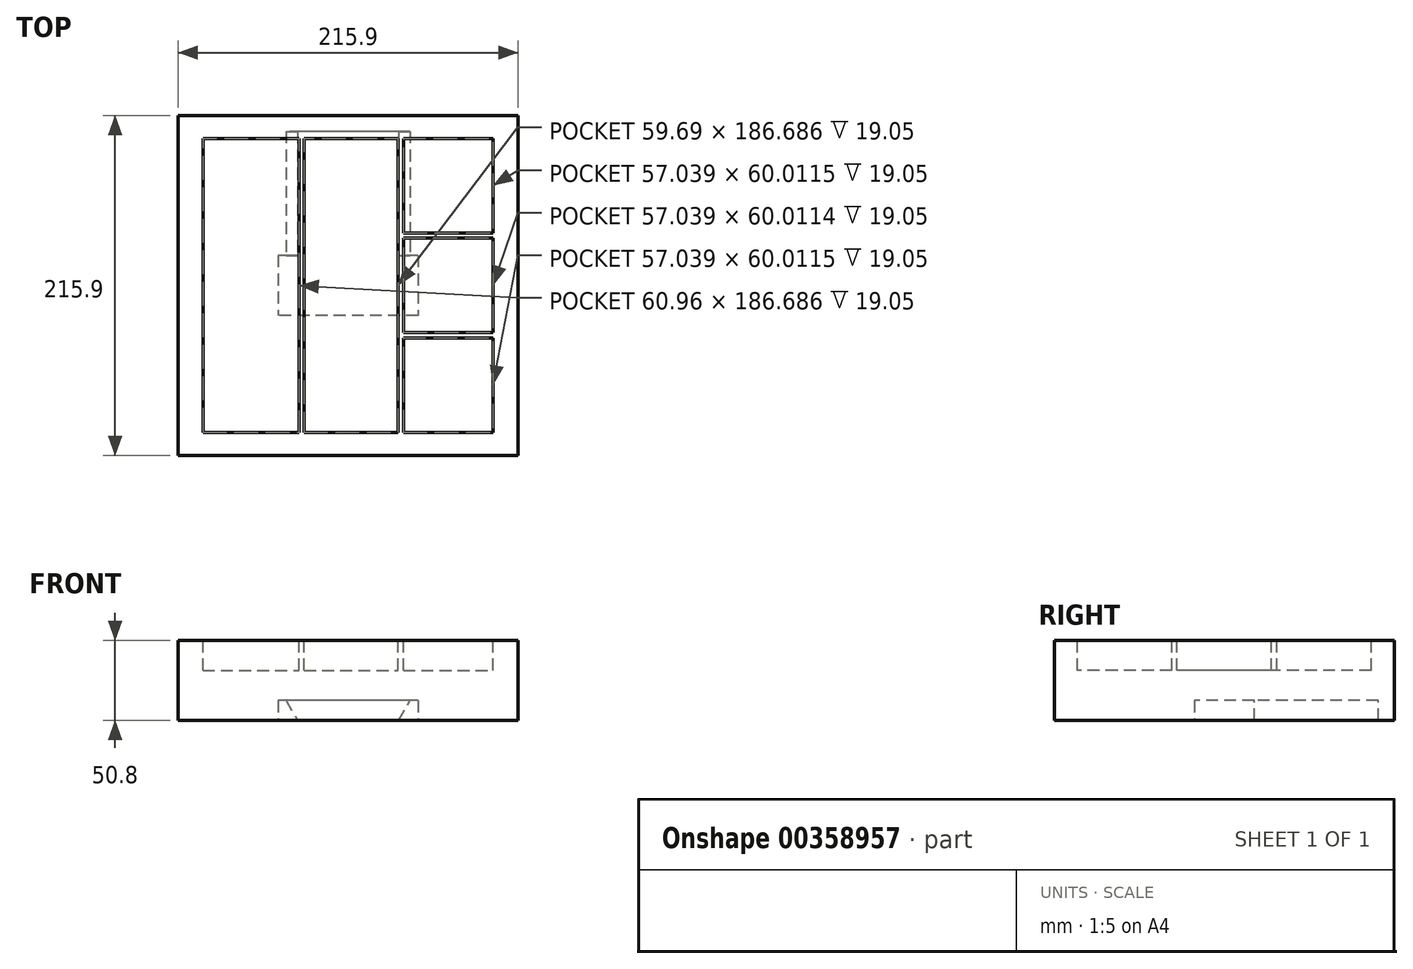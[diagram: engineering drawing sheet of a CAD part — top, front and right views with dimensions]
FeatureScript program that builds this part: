
annotation { "Feature Type Name" : "Feature", "Feature Type Description" : "" }
export const myFeature = defineFeature(function(context is Context, id is Id, definition is map)
    precondition{}
    {
        {
            var Q0;
            Q0=qCreatedBy(makeId("Top.planeOp"),FACE);
            var sketch = newSketch(context, id + "F0", { "sketchPlane" : qUnion([Q0])});
            skLineSegment(sketch, "E0.bottom", {"start": v(-107.95, 107.95) * mm, "end": v(107.95, 107.95) * mm});
            skLineSegment(sketch, "E0.top", {"start": v(-107.95, -107.95) * mm, "end": v(107.95, -107.95) * mm});
            skLineSegment(sketch, "E0.left", {"start": v(-107.95, 107.95) * mm, "end": v(-107.95, -107.95) * mm});
            skLineSegment(sketch, "E0.right", {"start": v(107.95, 107.95) * mm, "end": v(107.95, -107.95) * mm});
            skPoint(sketch, "E0.middle", {"position": v(0, 0) * mm});
            skSolve(sketch);
        }
        {
            var Q0;
            Q0 = qSketchRegion(id + "F0", true);
            extrude(context, id + "F1", {"entities" : qUnion([Q0]), "depth" : 50.8 * mm});
        }
        {
            var Q0;
            Q0=makeQuery(id+"F1.opExtrude","CAP_FACE",FACE,{"disambiguationData":[OSD([sQuery(id+"F0.wireOp",EDGE,"E0.bottom"),sQuery(id+"F0.wireOp",EDGE,"E0.top"),sQuery(id+"F0.wireOp",EDGE,"E0.left"),sQuery(id+"F0.wireOp",EDGE,"E0.right")])],"isStart":false});
            var sketch = newSketch(context, id + "F2", { "sketchPlane" : qUnion([Q0])});
            skLineSegment(sketch, "E1.bottom", {"start": v(-92.17, 93.34) * mm, "end": v(-31.21, 93.34) * mm});
            skLineSegment(sketch, "E1.top", {"start": v(-92.17, -93.34) * mm, "end": v(-31.21, -93.34) * mm});
            skLineSegment(sketch, "E1.left", {"start": v(-92.17, 93.34) * mm, "end": v(-92.17, -93.34) * mm});
            skLineSegment(sketch, "E1.right", {"start": v(92.17, 33.33) * mm, "end": v(92.17, 30) * mm});
            skPoint(sketch, "E1.middle", {"position": v(0, 0) * mm});
            skLineSegment(sketch, "E2", {"start": v(-31.21, 93.34) * mm, "end": v(-31.21, -93.34) * mm});
            skLineSegment(sketch, "E3", {"start": v(-27.88, 93.34) * mm, "end": v(-27.88, -93.34) * mm});
            skLineSegment(sketch, "E4", {"start": v(31.8, 93.34) * mm, "end": v(31.8, -93.34) * mm});
            skLineSegment(sketch, "E5", {"start": v(35.13, 93.34) * mm, "end": v(35.13, -93.34) * mm});
            skLineSegment(sketch, "E6.trimOffspring", {"start": v(-27.88, 93.34) * mm, "end": v(31.8, 93.34) * mm});
            skLineSegment(sketch, "E7.trimOffspring", {"start": v(-27.88, -93.34) * mm, "end": v(31.8, -93.34) * mm});
            skLineSegment(sketch, "E8.trimOffspring", {"start": v(35.13, -93.34) * mm, "end": v(92.17, -93.34) * mm});
            skLineSegment(sketch, "E9.trimOffspring", {"start": v(35.13, 93.34) * mm, "end": v(92.17, 93.34) * mm});
            skLineSegment(sketch, "E10", {"start": v(92.17, 33.33) * mm, "end": v(35.13, 33.33) * mm});
            skLineSegment(sketch, "E11", {"start": v(92.17, -30) * mm, "end": v(35.13, -30) * mm});
            skLineSegment(sketch, "E12", {"start": v(92.17, -30) * mm, "end": v(92.17, -33.33) * mm});
            skLineSegment(sketch, "E13", {"start": v(92.17, -33.33) * mm, "end": v(35.13, -33.33) * mm});
            skLineSegment(sketch, "E14", {"start": v(35.13, -33.33) * mm, "end": v(35.13, -30) * mm});
            skLineSegment(sketch, "E15", {"start": v(92.17, 30) * mm, "end": v(35.13, 30) * mm});
            skLineSegment(sketch, "E16", {"start": v(31.8, -93.34) * mm, "end": v(35.13, -93.34) * mm});
            skLineSegment(sketch, "E17", {"start": v(-27.88, -93.34) * mm, "end": v(-31.21, -93.34) * mm});
            skLineSegment(sketch, "E18.trimOffspring", {"start": v(92.17, -30) * mm, "end": v(92.17, -93.34) * mm});
            skLineSegment(sketch, "E19", {"start": v(92.17, 93.34) * mm, "end": v(92.17, -30) * mm});
            skLineSegment(sketch, "E20", {"start": v(35.13, 33.33) * mm, "end": v(35.13, 93.34) * mm});
            skLineSegment(sketch, "E21", {"start": v(35.13, -30) * mm, "end": v(35.13, 30) * mm});
            skLineSegment(sketch, "E22", {"start": v(35.13, -93.34) * mm, "end": v(35.13, -33.33) * mm});
            skSolve(sketch);
        }
        {
            var Q0;
            Q0=makeQuery(id+"F2.imprint","IMPRINT",FACE,{"disambiguationData":[TD([[makeQuery(id+"F2.imprint","IMPRINT",EDGE,{"derivedFrom":sQuery(id+"F2.wireOp",EDGE,"E1.bottom")}),-1.0]])]});
            var Q1;
            Q1=makeQuery(id+"F2.imprint","IMPRINT",FACE,{"disambiguationData":[TD([[makeQuery(id+"F2.imprint","IMPRINT",EDGE,{"derivedFrom":sQuery(id+"F2.wireOp",EDGE,"E3")}),1.0]])]});
            var Q2;
            {var subQ0=sQuery(id+"F2.wireOp",EDGE,"E9.trimOffspring");Q2=makeQuery(id+"F2.imprint","IMPRINT",FACE,{"disambiguationData":[TD([[makeQuery(id+"F2.imprint","IMPRINT",EDGE,{"derivedFrom":subQ0}),-1.0]])]});}
            var Q3;
            {var subQ0=sQuery(id+"F2.wireOp",EDGE,"E11");Q3=makeQuery(id+"F2.imprint","IMPRINT",FACE,{"disambiguationData":[TD([[makeQuery(id+"F2.imprint","IMPRINT",EDGE,{"derivedFrom":subQ0}),-1.0]])]});}
            var Q4;
            {var subQ0=sQuery(id+"F2.wireOp",EDGE,"E8.trimOffspring");Q4=makeQuery(id+"F2.imprint","IMPRINT",FACE,{"disambiguationData":[TD([[makeQuery(id+"F2.imprint","IMPRINT",EDGE,{"derivedFrom":subQ0}),1.0]])]});}
            extrude(context, id + "F3", {"entities" : qUnion([Q0, Q1, Q2, Q3, Q4]), "operationType" : NewBodyOperationType.REMOVE, "oppositeDirection" : true, "depth" : 19.05 * mm});
        }
        {
            var Q0;
            Q0=makeQuery(id+"F1.opExtrude","CAP_FACE",FACE,{"disambiguationData":[OSD([sQuery(id+"F0.wireOp",EDGE,"E0.bottom"),sQuery(id+"F0.wireOp",EDGE,"E0.top"),sQuery(id+"F0.wireOp",EDGE,"E0.left"),sQuery(id+"F0.wireOp",EDGE,"E0.right")])],"isStart":true});
            var sketch = newSketch(context, id + "F4", { "sketchPlane" : qUnion([Q0])});
            skLineSegment(sketch, "E23.bottom", {"start": v(44.45, -19.05) * mm, "end": v(-44.45, -19.05) * mm});
            skLineSegment(sketch, "E23.top", {"start": v(44.45, 19.05) * mm, "end": v(-44.45, 19.05) * mm});
            skLineSegment(sketch, "E23.left", {"start": v(44.45, -19.05) * mm, "end": v(44.45, 19.05) * mm});
            skLineSegment(sketch, "E23.right", {"start": v(-44.45, -19.05) * mm, "end": v(-44.45, 19.05) * mm});
            skPoint(sketch, "E23.middle", {"position": v(0, 0) * mm});
            skSolve(sketch);
        }
        {
            var Q0;
            Q0 = qSketchRegion(id + "F4", true);
            extrude(context, id + "F5", {"entities" : qUnion([Q0]), "operationType" : NewBodyOperationType.REMOVE, "oppositeDirection" : true, "depth" : 12.7 * mm});
        }
        {
            var Q0;
            Q0=makeQuery(id+"F5.boolean.opBoolean","COPY",FACE,{"derivedFrom":makeQuery(id+"F5.opExtrude","SWEPT_FACE",FACE,{"disambiguationData":[OSD([sQuery(id+"F4.wireOp",EDGE,"E23.bottom")])]})});
            var sketch = newSketch(context, id + "F6", { "sketchPlane" : qUnion([Q0])});
            skLineSegment(sketch, "E24", {"start": v(0, 0) * mm, "end": v(32.13, 0) * mm});
            skLineSegment(sketch, "E25", {"start": v(32.13, 0) * mm, "end": v(39.42, 12.7) * mm});
            skLineSegment(sketch, "E26", {"start": v(39.42, 12.7) * mm, "end": v(-39.42, 12.7) * mm});
            skLineSegment(sketch, "E27", {"start": v(-39.42, 12.7) * mm, "end": v(-32.13, 0) * mm});
            skLineSegment(sketch, "E28", {"start": v(-32.13, 0) * mm, "end": v(0, 0) * mm});
            skLineSegment(sketch, "E29", {"start": v(32.13, 0) * mm, "end": v(0, 0) * mm});
            skSolve(sketch);
        }
        {
            var Q0;
            Q0 = qSketchRegion(id + "F6", true);
            extrude(context, id + "F7", {"entities" : qUnion([Q0]), "operationType" : NewBodyOperationType.REMOVE, "oppositeDirection" : true, "depth" : 78.74 * mm});
        }
    });
